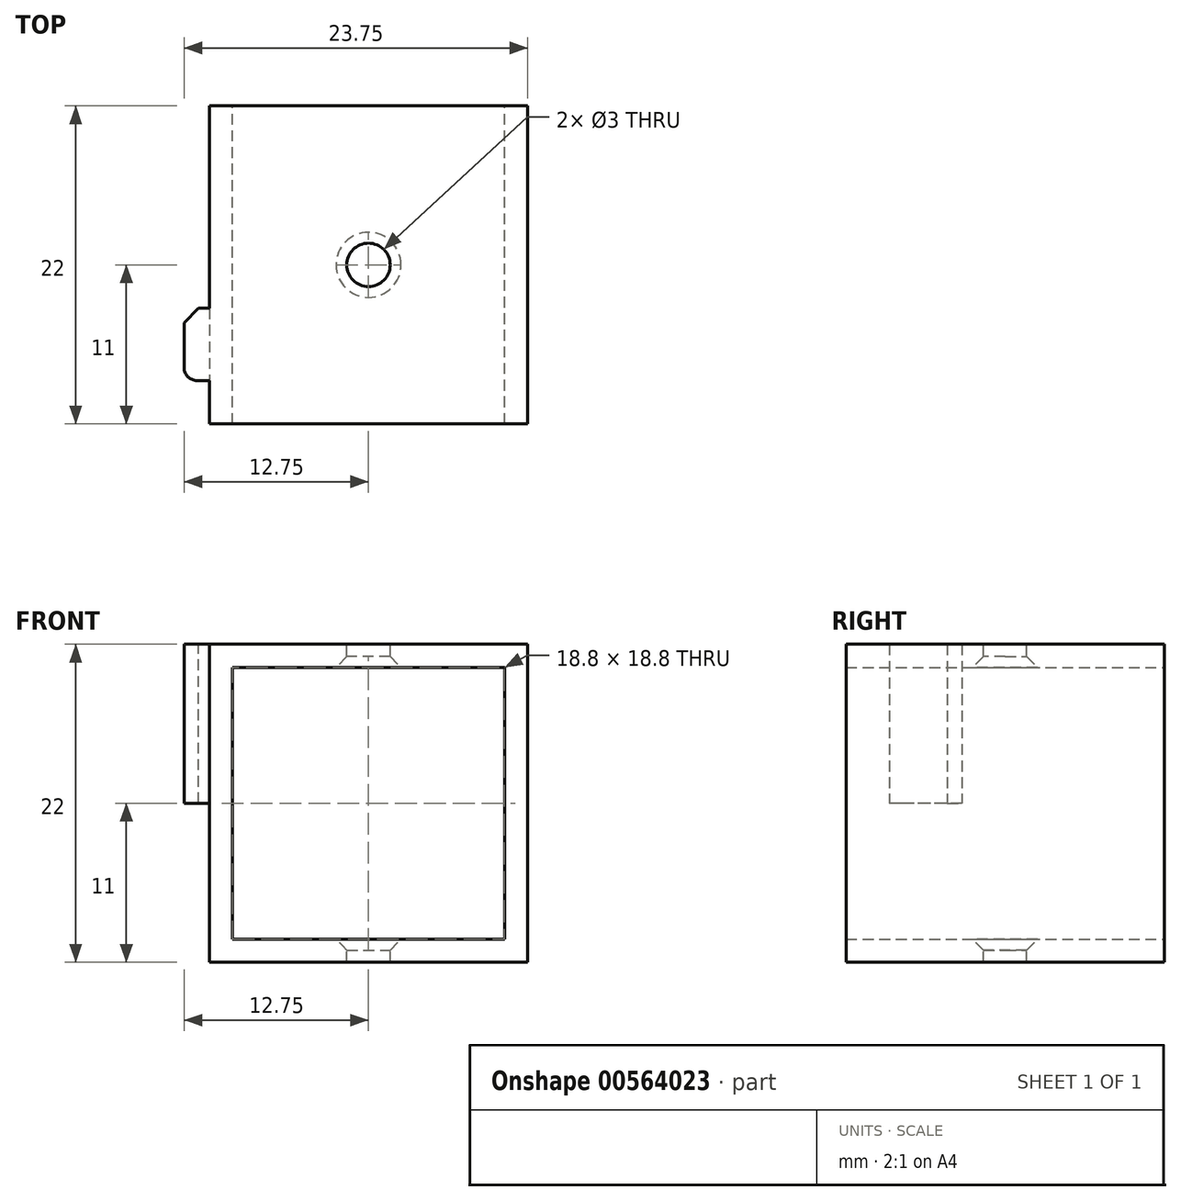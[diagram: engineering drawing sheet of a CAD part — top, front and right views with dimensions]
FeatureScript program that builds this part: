
annotation { "Feature Type Name" : "Feature", "Feature Type Description" : "" }
export const myFeature = defineFeature(function(context is Context, id is Id, definition is map)
    precondition{}
    {
        {
            var Q0;
            Q0=qCreatedBy(makeId("Front.planeOp"),FACE);
            var sketch = newSketch(context, id + "F0", { "sketchPlane" : qUnion([Q0])});
            skLineSegment(sketch, "E0.bottom", {"start": v(9.4, -9.4) * mm, "end": v(-9.4, -9.4) * mm});
            skLineSegment(sketch, "E0.top", {"start": v(9.4, 9.4) * mm, "end": v(-9.4, 9.4) * mm});
            skLineSegment(sketch, "E0.left", {"start": v(9.4, -9.4) * mm, "end": v(9.4, 9.4) * mm});
            skLineSegment(sketch, "E0.right", {"start": v(-9.4, -9.4) * mm, "end": v(-9.4, 9.4) * mm});
            skPoint(sketch, "E0.middle", {"position": v(0, 0) * mm});
            skLineSegment(sketch, "E1.bottom", {"start": v(11, -11) * mm, "end": v(-11, -11) * mm});
            skLineSegment(sketch, "E1.top", {"start": v(11, 11) * mm, "end": v(-11, 11) * mm});
            skLineSegment(sketch, "E1.left", {"start": v(11, -11) * mm, "end": v(11, 11) * mm});
            skLineSegment(sketch, "E1.right", {"start": v(-11, -11) * mm, "end": v(-11, 11) * mm});
            skSolve(sketch);
        }
        {
            var Q0;
            Q0 = qSketchRegion(id + "F0", true);
            extrude(context, id + "F1", {"entities" : qUnion([Q0]), "endBound" : BoundingType.SYMMETRIC, "depth" : 22 * mm, "offsetDistance" : 25 * mm});
        }
        {
            var Q0;
            Q0=makeQuery(id+"F1.opExtrude","SWEPT_FACE",FACE,{"disambiguationData":[OSD([sQuery(id+"F0.wireOp",EDGE,"E1.top")])]});
            var sketch = newSketch(context, id + "F2", { "sketchPlane" : qUnion([Q0])});
            skLineSegment(sketch, "E2", {"start": v(0, 11) * mm, "end": v(0, -11) * mm, "construction": true});
            skCircle(sketch, "E3", {"center": v(0, 0) * mm, "radius": 1.5 * mm});
            skSolve(sketch);
        }
        {
            var Q0;
            Q0 = qSketchRegion(id + "F2", true);
            extrude(context, id + "F3", {"entities" : qUnion([Q0]), "operationType" : NewBodyOperationType.REMOVE, "oppositeDirection" : true, "depth" : 25 * mm, "offsetDistance" : 25 * mm});
        }
        {
            var Q0;
            Q0=makeQuery(id+"F3.boolean.opBoolean","INTERSECT",EDGE,{"derivedFrom":[makeQuery(id+"F1.opExtrude","SWEPT_FACE",FACE,{"disambiguationData":[OSD([sQuery(id+"F0.wireOp",EDGE,"E0.bottom")])]}),makeQuery(id+"F3.opExtrude","SWEPT_FACE",FACE,{"disambiguationData":[OSD([sQuery(id+"F2.wireOp",EDGE,"E3")])]})]});
            var Q1;
            Q1=makeQuery(id+"F3.boolean.opBoolean","INTERSECT",EDGE,{"derivedFrom":[makeQuery(id+"F1.opExtrude","SWEPT_FACE",FACE,{"disambiguationData":[OSD([sQuery(id+"F0.wireOp",EDGE,"E0.top")])]}),makeQuery(id+"F3.opExtrude","SWEPT_FACE",FACE,{"disambiguationData":[OSD([sQuery(id+"F2.wireOp",EDGE,"E3")])]})]});
            chamfer(context, id + "F4", {"entities" : qUnion([Q0, Q1]), "width" : 0.75 * mm, "tangentPropagation" : true});
        }
        {
            var Q0;
            Q0=qCreatedBy(makeId("Top.planeOp"),FACE);
            var sketch = newSketch(context, id + "F5", { "sketchPlane" : qUnion([Q0])});
            skLineSegment(sketch, "E4.bottom", {"start": v(-15, -3) * mm, "end": v(-11, -3) * mm});
            skLineSegment(sketch, "E4.top", {"start": v(-15, -11) * mm, "end": v(-11, -11) * mm});
            skLineSegment(sketch, "E4.left", {"start": v(-15, -3) * mm, "end": v(-15, -11) * mm});
            skLineSegment(sketch, "E4.right", {"start": v(-11, -3) * mm, "end": v(-11, -11) * mm});
            skLineSegment(sketch, "E5.bottom", {"start": v(-11, -3) * mm, "end": v(-12.75, -3) * mm});
            skLineSegment(sketch, "E5.top", {"start": v(-11, -8) * mm, "end": v(-12.75, -8) * mm});
            skLineSegment(sketch, "E5.left", {"start": v(-11, -3) * mm, "end": v(-11, -8) * mm});
            skLineSegment(sketch, "E5.right", {"start": v(-12.75, -3) * mm, "end": v(-12.75, -8) * mm});
            skPoint(sketch, "E6", {"position": v(-15, -8) * mm});
            skSolve(sketch);
        }
        {
            var Q0;
            Q0=makeQuery(id+"F5.imprint","IMPRINT",FACE,{"disambiguationData":[TD([[makeQuery(id+"F5.imprint","IMPRINT",EDGE,{"derivedFrom":sQuery(id+"F5.wireOp",EDGE,"E4.bottom")}),-1.0]])]});
            var Q1;
            Q1=makeQuery(id+"F1.opExtrude","SWEPT_FACE",FACE,{"disambiguationData":[OSD([sQuery(id+"F0.wireOp",EDGE,"E1.top")])]});
            extrude(context, id + "F6", {"entities" : qUnion([Q0]), "operationType" : NewBodyOperationType.ADD, "endBound" : BoundingType.UP_TO_SURFACE, "depth" : 25 * mm, "endBoundEntityFace" : qUnion([Q1]), "offsetDistance" : 25 * mm});
        }
        {
            var Q0;
            Q0=makeQuery(id+"F6.opExtrude","SWEPT_EDGE",EDGE,{"disambiguationData":[OSD([sQuery(id+"F5.wireOp",EDGE,"E5.top"),sQuery(id+"F5.wireOp",EDGE,"E5.right")])]});
            var Q1;
            Q1=makeQuery(id+"F6.opExtrude","SWEPT_EDGE",EDGE,{"disambiguationData":[OSD([sQuery(id+"F5.wireOp",EDGE,"E4.right"),sQuery(id+"F5.wireOp",EDGE,"E5.top"),sQuery(id+"F5.wireOp",EDGE,"E5.left")])]});
            fillet(context, id + "F7", {"entities" : qUnion([Q0, Q1]), "radius" : (1.75 / 2) * mm, "tangentPropagation" : true, "allowEdgeOverflow" : false});
        }
        {
            var Q0;
            Q0=makeQuery(id+"F6.opExtrude","SWEPT_EDGE",EDGE,{"disambiguationData":[OSD([sQuery(id+"F5.wireOp",EDGE,"E4.bottom"),sQuery(id+"F5.wireOp",EDGE,"E5.bottom"),sQuery(id+"F5.wireOp",EDGE,"E5.right")])]});
            chamfer(context, id + "F8", {"entities" : qUnion([Q0]), "width" : 1 * mm, "tangentPropagation" : true});
        }
    });
